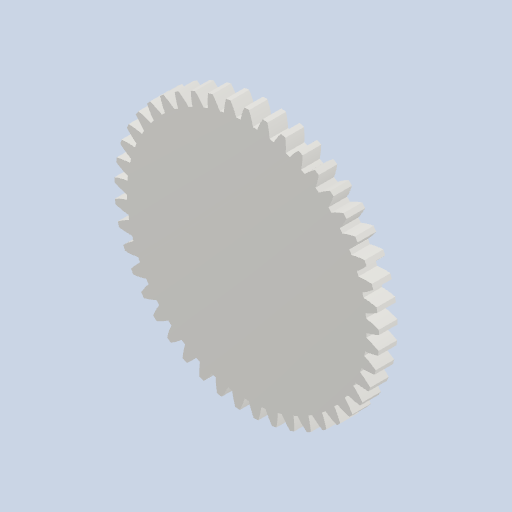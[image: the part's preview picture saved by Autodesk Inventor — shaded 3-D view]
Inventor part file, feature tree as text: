
AUTODESK INVENTOR PART (.ipt)
format: ipt  version: 2022 (Build 260153000, 153)  size: 323,584 bytes
history: native  units: mm (DEFAULTED — no unit token found)
features: plane x3, other x3, sketch x2, extrude x1
ambient origin geometry x8: Origin, YZ Plane, XZ Plane, XY Plane, X Axis, Y Axis, Z Axis, Center Point
bodies: Solid1 (feature_tree)
feature tree (9):
  extrude  "Extrusion1"  Depth=5.0mm TaperAngle=0.0deg
  plane  "Work Plane2"
  plane  "Work Plane8"
  plane  "Work Plane9"
  other  "Цилиндрическое зубчатое зацепление"
  sketch  "Sketch1"  dims[d0=71.341203mm d1=5.0mm d2=0.0mm]
  sketch  "Sketch2"  dims[d3=67.5mm d4=10.0mm d5=0.0mm d16=43.170602mm d17=0.0mm d34=0.698132mm d39=0.0mm d41=0.0mm d43=43.170602mm d46=43.170602mm d47=0.0mm d48=0.0mm]
  other  "Srf1"
  other  "Средний диаметр"
